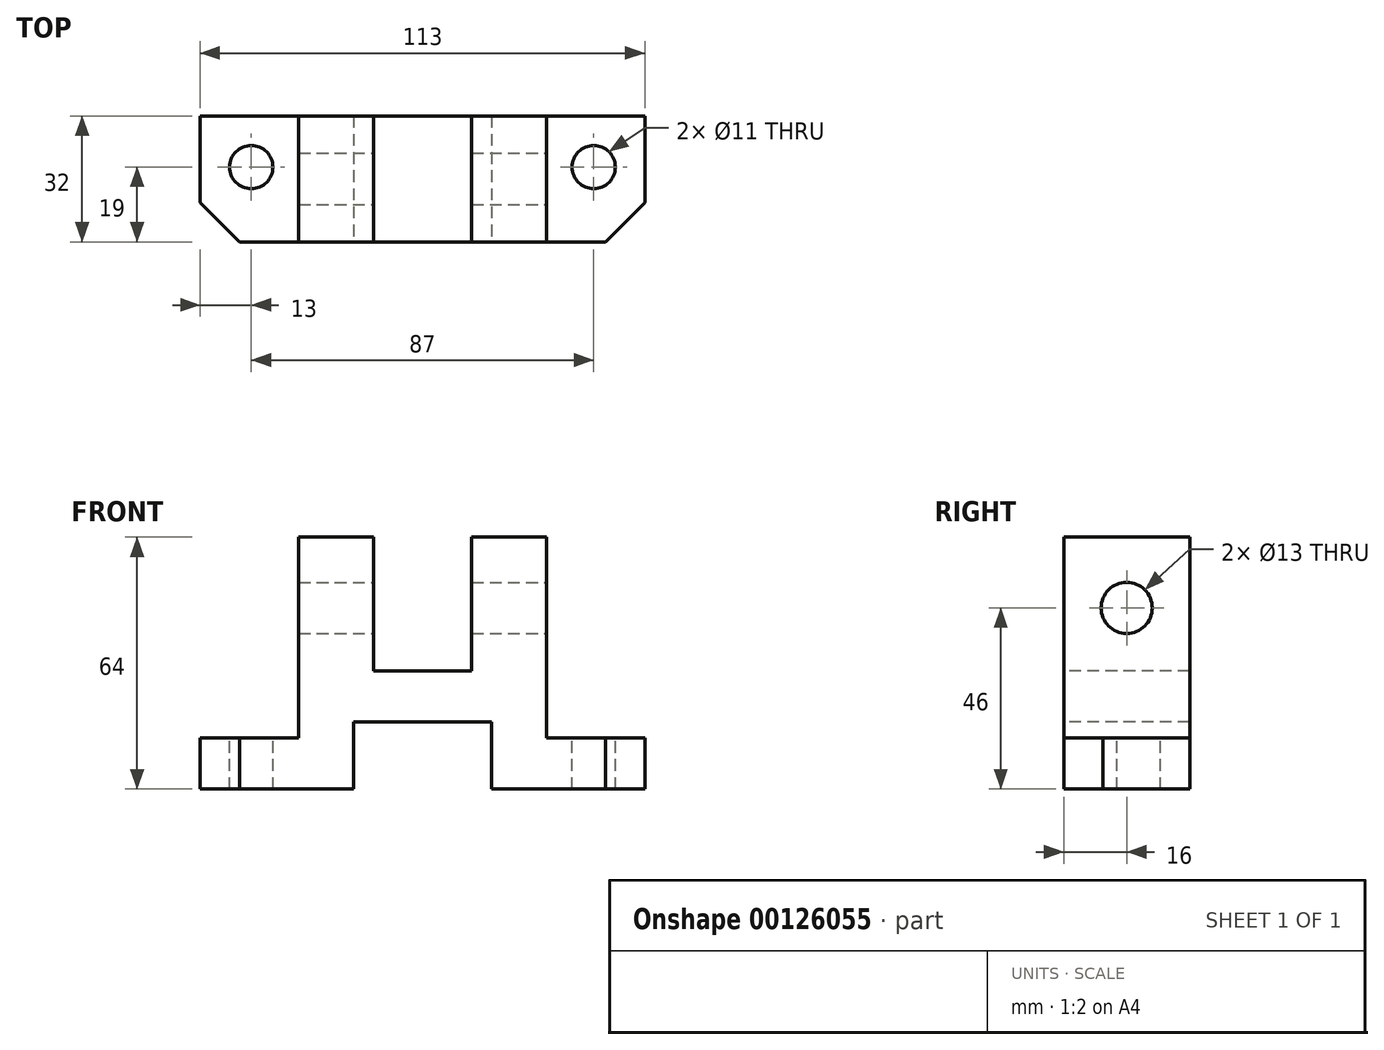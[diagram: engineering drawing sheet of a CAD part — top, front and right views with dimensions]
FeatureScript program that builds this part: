
annotation { "Feature Type Name" : "Feature", "Feature Type Description" : "" }
export const myFeature = defineFeature(function(context is Context, id is Id, definition is map)
    precondition{}
    {
        {
            var Q0;
            Q0=qCreatedBy(makeId("Front.planeOp"),FACE);
            var sketch = newSketch(context, id + "F0", { "sketchPlane" : qUnion([Q0])});
            skLineSegment(sketch, "E0", {"start": v(0, 0) * mm, "end": v(0, 13) * mm});
            skLineSegment(sketch, "E1", {"start": v(0, 13) * mm, "end": v(-25, 13) * mm});
            skLineSegment(sketch, "E2", {"start": v(-25, 13) * mm, "end": v(-25, 64) * mm});
            skLineSegment(sketch, "E3", {"start": v(-25, 64) * mm, "end": v(-44, 64) * mm});
            skLineSegment(sketch, "E4", {"start": v(-69, 64) * mm, "end": v(-88, 64) * mm});
            skLineSegment(sketch, "E5", {"start": v(-88, 64) * mm, "end": v(-88, 13) * mm});
            skLineSegment(sketch, "E6", {"start": v(-88, 13) * mm, "end": v(-113, 13) * mm});
            skLineSegment(sketch, "E7", {"start": v(-113, 13) * mm, "end": v(-113, 0) * mm});
            skLineSegment(sketch, "E8", {"start": v(-113, 0) * mm, "end": v(-74, 0) * mm});
            skLineSegment(sketch, "E9", {"start": v(-74, 0) * mm, "end": v(-74, 17) * mm});
            skLineSegment(sketch, "E10", {"start": v(-74, 17) * mm, "end": v(-39, 17) * mm});
            skLineSegment(sketch, "E11", {"start": v(-39, 17) * mm, "end": v(-39, 0) * mm});
            skLineSegment(sketch, "E12", {"start": v(-39, 0) * mm, "end": v(0, 0) * mm});
            skLineSegment(sketch, "E13", {"start": v(-69, 64) * mm, "end": v(-69, 30) * mm});
            skLineSegment(sketch, "E14", {"start": v(-69, 30) * mm, "end": v(-44, 30) * mm});
            skLineSegment(sketch, "E15", {"start": v(-44, 30) * mm, "end": v(-44, 64) * mm});
            skSolve(sketch);
        }
        {
            var Q0;
            Q0 = qSketchRegion(id + "F0", true);
            extrude(context, id + "F1", {"entities" : qUnion([Q0]), "oppositeDirection" : true, "depth" : 32 * mm});
        }
        {
            var Q0;
            Q0=makeQuery(id+"F1.opExtrude","SWEPT_FACE",FACE,{"disambiguationData":[OSD([sQuery(id+"F0.wireOp",EDGE,"E1")])]});
            var sketch = newSketch(context, id + "F2", { "sketchPlane" : qUnion([Q0])});
            skCircle(sketch, "E16", {"center": v(-13, 19) * mm, "radius": 5.5 * mm});
            skCircle(sketch, "E17", {"center": v(-100, 19) * mm, "radius": 5.5 * mm});
            skSolve(sketch);
        }
        {
            var Q0;
            Q0 = qSketchRegion(id + "F2", true);
            extrude(context, id + "F3", {"entities" : qUnion([Q0]), "operationType" : NewBodyOperationType.REMOVE, "endBound" : BoundingType.THROUGH_ALL, "oppositeDirection" : true, "depth" : 25 * mm});
        }
        {
            var Q0;
            Q0=makeQuery(id+"F1.opExtrude","SWEPT_FACE",FACE,{"disambiguationData":[OSD([sQuery(id+"F0.wireOp",EDGE,"E6")])]});
            var sketch = newSketch(context, id + "F4", { "sketchPlane" : qUnion([Q0])});
            skLineSegment(sketch, "E18", {"start": v(-113, 0) * mm, "end": v(-103, 0) * mm});
            skLineSegment(sketch, "E19", {"start": v(-113, 0) * mm, "end": v(-113, 10) * mm});
            skLineSegment(sketch, "E20", {"start": v(-113, 10) * mm, "end": v(-103, 0) * mm});
            skLineSegment(sketch, "E21", {"start": v(0, 0) * mm, "end": v(-10, 0) * mm});
            skLineSegment(sketch, "E22", {"start": v(-10, 0) * mm, "end": v(0, 10) * mm});
            skLineSegment(sketch, "E23", {"start": v(0, 10) * mm, "end": v(0, 0) * mm});
            skSolve(sketch);
        }
        {
            var Q0;
            Q0 = qSketchRegion(id + "F4", true);
            extrude(context, id + "F5", {"entities" : qUnion([Q0]), "operationType" : NewBodyOperationType.REMOVE, "endBound" : BoundingType.THROUGH_ALL, "oppositeDirection" : true, "depth" : 25 * mm});
        }
        {
            var Q0;
            Q0=makeQuery(id+"F1.opExtrude","SWEPT_FACE",FACE,{"disambiguationData":[OSD([sQuery(id+"F0.wireOp",EDGE,"E2")])]});
            var sketch = newSketch(context, id + "F6", { "sketchPlane" : qUnion([Q0])});
            skCircle(sketch, "E24", {"center": v(16, 46) * mm, "radius": 6.5 * mm});
            skSolve(sketch);
        }
        {
            var Q0;
            Q0 = qSketchRegion(id + "F6", true);
            extrude(context, id + "F7", {"entities" : qUnion([Q0]), "operationType" : NewBodyOperationType.REMOVE, "endBound" : BoundingType.THROUGH_ALL, "oppositeDirection" : true, "depth" : 25 * mm});
        }
    });
